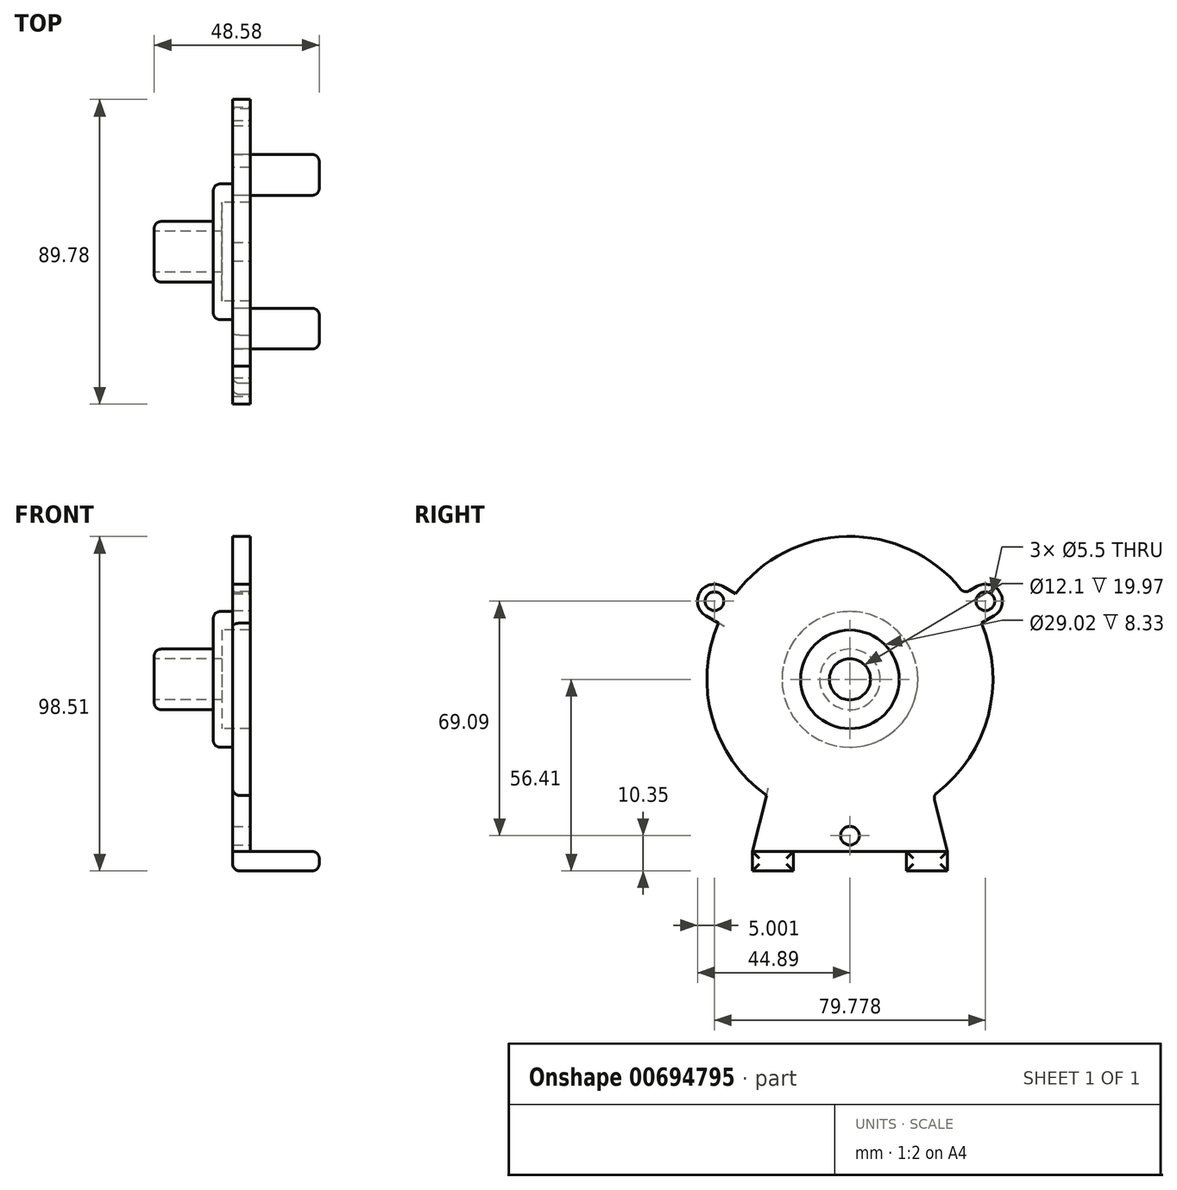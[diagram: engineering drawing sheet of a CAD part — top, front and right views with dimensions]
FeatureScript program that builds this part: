
annotation { "Feature Type Name" : "Feature", "Feature Type Description" : "" }
export const myFeature = defineFeature(function(context is Context, id is Id, definition is map)
    precondition{}
    {
        {
            var Q0;
            Q0=qCreatedBy(makeId("Front.planeOp"),FACE);
            var sketch = newSketch(context, id + "F0", { "sketchPlane" : qUnion([Q0])});
            skLineSegment(sketch, "E0", {"start": v(0, 42.1) * mm, "end": v(-5.2, 42.1) * mm});
            skLineSegment(sketch, "E1", {"start": v(-5.2, 42.1) * mm, "end": v(-5.2, 20) * mm});
            skLineSegment(sketch, "E2", {"start": v(-5.2, 20) * mm, "end": v(-10.9, 20) * mm});
            skLineSegment(sketch, "E3", {"start": v(-10.9, 20) * mm, "end": v(-10.9, 8.92) * mm});
            skLineSegment(sketch, "E4", {"start": v(-10.9, 8.93) * mm, "end": v(-28.3, 8.92) * mm});
            skLineSegment(sketch, "E5", {"start": v(-28.3, 8.92) * mm, "end": v(-28.3, 6.05) * mm});
            skLineSegment(sketch, "E6", {"start": v(-28.3, 6.05) * mm, "end": v(-8.33, 6.05) * mm});
            skLineSegment(sketch, "E7", {"start": v(-8.33, 6.05) * mm, "end": v(-8.33, 14.5) * mm});
            skLineSegment(sketch, "E8", {"start": v(-8.33, 14.5) * mm, "end": v(0, 14.5) * mm});
            skLineSegment(sketch, "E9", {"start": v(0, 14.51) * mm, "end": v(0, 42.1) * mm});
            skLineSegment(sketch, "E10.MirrorCS", {"start": v(-28.3, -8.92) * mm, "end": v(-28.3, -6.05) * mm});
            skLineSegment(sketch, "E11.MirrorCS", {"start": v(0, -14.51) * mm, "end": v(0, -42.1) * mm});
            skLineSegment(sketch, "E12.MirrorCS", {"start": v(-8.33, -14.5) * mm, "end": v(0, -14.5) * mm});
            skLineSegment(sketch, "E13.MirrorCS", {"start": v(-8.33, -6.05) * mm, "end": v(-8.33, -14.5) * mm});
            skLineSegment(sketch, "E14.MirrorCS", {"start": v(-10.9, -20) * mm, "end": v(-10.9, -8.92) * mm});
            skLineSegment(sketch, "E15.MirrorCS", {"start": v(-5.2, -20) * mm, "end": v(-10.9, -20) * mm});
            skLineSegment(sketch, "E16.MirrorCS", {"start": v(-28.3, -6.05) * mm, "end": v(-8.33, -6.05) * mm});
            skLineSegment(sketch, "E17.MirrorCS", {"start": v(-5.2, -42.1) * mm, "end": v(-5.2, -20) * mm});
            skLineSegment(sketch, "E18.MirrorCS", {"start": v(0, -42.1) * mm, "end": v(-5.2, -42.1) * mm});
            skLineSegment(sketch, "E19.MirrorCS", {"start": v(-10.9, -8.93) * mm, "end": v(-28.3, -8.92) * mm});
            skLineSegment(sketch, "E20", {"start": v(-5.2, -42.1) * mm, "end": v(-5.2, -56.41) * mm});
            skLineSegment(sketch, "E21", {"start": v(20.28, -50.7) * mm, "end": v(0, -50.71) * mm});
            skLineSegment(sketch, "E22", {"start": v(20.28, -50.7) * mm, "end": v(20.28, -56.41) * mm});
            skLineSegment(sketch, "E23", {"start": v(-5.2, -56.41) * mm, "end": v(20.28, -56.41) * mm});
            skLineSegment(sketch, "E24", {"start": v(0, -50.71) * mm, "end": v(0, -42.1) * mm});
            skLineSegment(sketch, "E25", {"start": v(-50.44, 0) * mm, "end": v(37.55, 0) * mm});
            skLineSegment(sketch, "E26", {"start": v(-5.2, -20) * mm, "end": v(-5.2, -14.5) * mm});
            skSolve(sketch);
        }
        {
            var Q0;
            Q0=makeQuery(id+"F0.imprint","IMPRINT",FACE,{"disambiguationData":[TD([[makeQuery(id+"F0.imprint","IMPRINT",EDGE,{"derivedFrom":sQuery(id+"F0.wireOp",EDGE,"E0")}),1.0]])]});
            var Q1;
            Q1=sQuery(id+"F0.wireOp",EDGE,"E25");
            revolve(context, id + "F1", {"entities" : qUnion([Q0]), "axis" : qUnion([Q1]), "revolveType" : RevolveType.FULL});
        }
        {
            var Q0;
            Q0=qCreatedBy(makeId("Right.planeOp"),FACE);
            var sketch = newSketch(context, id + "F2", { "sketchPlane" : qUnion([Q0])});
            skArc(sketch, "E27", {"start": v(-33.7, 25.23) * mm, "mid": v(-36.46, 21.05) * mm, "end": v(-38.7, 16.57) * mm});
            skArc(sketch, "E28", {"start": v(-37.39, 27.36) * mm, "mid": v(-44.22, 25.53) * mm, "end": v(-42.39, 18.7) * mm});
            skLineSegment(sketch, "E29", {"start": v(-37.39, 27.36) * mm, "end": v(-33.7, 25.23) * mm});
            skLineSegment(sketch, "E30", {"start": v(-42.39, 18.7) * mm, "end": v(-38.7, 16.57) * mm});
            skLineSegment(sketch, "E31", {"start": v(-39.89, 23.03) * mm, "end": v(0, 0) * mm, "construction": true});
            skCircle(sketch, "E32", {"center": v(-39.89, 23.03) * mm, "radius": 2.75 * mm});
            skLineSegment(sketch, "E33.MirrorCS", {"start": v(42.39, 18.7) * mm, "end": v(38.7, 16.57) * mm});
            skArc(sketch, "E34.MirrorCS", {"start": v(33.7, 25.23) * mm, "mid": v(36.46, 21.05) * mm, "end": v(38.7, 16.57) * mm});
            skArc(sketch, "E35.MirrorCS", {"start": v(37.39, 27.36) * mm, "mid": v(44.22, 25.53) * mm, "end": v(42.39, 18.7) * mm});
            skLineSegment(sketch, "E36.MirrorCS", {"start": v(37.39, 27.36) * mm, "end": v(33.7, 25.23) * mm});
            skCircle(sketch, "E37.MirrorC", {"center": v(39.89, 23.03) * mm, "radius": 2.75 * mm});
            skLineSegment(sketch, "E38.MirrorCS", {"start": v(39.89, 23.03) * mm, "end": v(0, 0) * mm, "construction": true});
            skCircle(sketch, "E39", {"center": v(0, -46.06) * mm, "radius": 2.75 * mm});
            skCircle(sketch, "E40", {"center": v(0, 0) * mm, "radius": 46.06 * mm, "construction": true});
            skLineSegment(sketch, "E41", {"start": v(-24.57, -34.19) * mm, "end": v(-28.65, -50.71) * mm});
            skLineSegment(sketch, "E42", {"start": v(-28.65, -50.71) * mm, "end": v(-28.65, -56.41) * mm});
            skLineSegment(sketch, "E43", {"start": v(-28.65, -56.41) * mm, "end": v(-16.65, -56.41) * mm});
            skLineSegment(sketch, "E44", {"start": v(-28.65, -50.71) * mm, "end": v(28.65, -50.71) * mm});
            skLineSegment(sketch, "E45.MirrorCS", {"start": v(24.57, -34.19) * mm, "end": v(28.65, -50.71) * mm});
            skLineSegment(sketch, "E46.MirrorCS", {"start": v(28.65, -50.71) * mm, "end": v(28.65, -56.41) * mm});
            skArc(sketch, "E47", {"start": v(-24.57, -34.19) * mm, "mid": v(0, -42.1) * mm, "end": v(24.57, -34.19) * mm});
            skLineSegment(sketch, "E48", {"start": v(-16.65, -50.71) * mm, "end": v(-16.65, -56.41) * mm});
            skLineSegment(sketch, "E49.MirrorCS", {"start": v(16.65, -50.71) * mm, "end": v(16.65, -56.41) * mm});
            skLineSegment(sketch, "E50.trimOffspring", {"start": v(16.65, -56.41) * mm, "end": v(28.65, -56.41) * mm});
            skSolve(sketch);
        }
        {
            var Q0;
            Q0=makeQuery(id+"F2.imprint","IMPRINT",FACE,{"disambiguationData":[TD([[makeQuery(id+"F2.imprint","IMPRINT",EDGE,{"derivedFrom":sQuery(id+"F2.wireOp",EDGE,"E27")}),-1.0]])]});
            var Q1;
            Q1=makeQuery(id+"F1.opRevolve","SWEPT_FACE",FACE,{"disambiguationData":[OSD([sQuery(id+"F0.wireOp",EDGE,"E1")])]});
            extrude(context, id + "F3", {"entities" : qUnion([Q0]), "operationType" : NewBodyOperationType.ADD, "endBound" : BoundingType.UP_TO_SURFACE, "oppositeDirection" : true, "endBoundEntityFace" : qUnion([Q1]), "depth" : 25 * mm});
        }
        {
            var Q0;
            Q0=makeQuery(id+"F2.imprint","IMPRINT",FACE,{"disambiguationData":[TD([[makeQuery(id+"F2.imprint","IMPRINT",EDGE,{"derivedFrom":sQuery(id+"F2.wireOp",EDGE,"E33.MirrorCS")}),-1.0]])]});
            var Q1;
            Q1=makeQuery(id+"F3.boolean.opBoolean","MERGE",FACE,{"derivedFrom":[makeQuery(id+"F1.opRevolve","SWEPT_FACE",FACE,{"disambiguationData":[OSD([sQuery(id+"F0.wireOp",EDGE,"E1")])]}),makeQuery(id+"F3.opExtrude","CAP_FACE",FACE,{"disambiguationData":[OSD([sQuery(id+"F2.wireOp",EDGE,"E27"),sQuery(id+"F2.wireOp",EDGE,"E28"),sQuery(id+"F2.wireOp",EDGE,"E29"),sQuery(id+"F2.wireOp",EDGE,"E30"),sQuery(id+"F2.wireOp",EDGE,"E32")])],"isStart":false})]});
            extrude(context, id + "F4", {"entities" : qUnion([Q0]), "operationType" : NewBodyOperationType.ADD, "endBound" : BoundingType.UP_TO_SURFACE, "oppositeDirection" : true, "endBoundEntityFace" : qUnion([Q1]), "depth" : 25 * mm});
        }
        {
            var Q0;
            Q0=makeQuery(id+"F2.imprint","IMPRINT",FACE,{"disambiguationData":[TD([[makeQuery(id+"F2.imprint","IMPRINT",EDGE,{"derivedFrom":sQuery(id+"F2.wireOp",EDGE,"E39")}),-1.0]])]});
            var Q1;
            Q1=makeQuery(id+"F4.boolean.opBoolean","MERGE",FACE,{"derivedFrom":[makeQuery(id+"F3.boolean.opBoolean","MERGE",FACE,{"derivedFrom":[makeQuery(id+"F1.opRevolve","SWEPT_FACE",FACE,{"disambiguationData":[OSD([sQuery(id+"F0.wireOp",EDGE,"E1")])]}),makeQuery(id+"F3.opExtrude","CAP_FACE",FACE,{"disambiguationData":[OSD([sQuery(id+"F2.wireOp",EDGE,"E27"),sQuery(id+"F2.wireOp",EDGE,"E28"),sQuery(id+"F2.wireOp",EDGE,"E29"),sQuery(id+"F2.wireOp",EDGE,"E30"),sQuery(id+"F2.wireOp",EDGE,"E32")])],"isStart":false})]}),makeQuery(id+"F4.opExtrude","CAP_FACE",FACE,{"disambiguationData":[OSD([sQuery(id+"F2.wireOp",EDGE,"E33.MirrorCS"),sQuery(id+"F2.wireOp",EDGE,"E34.MirrorCS"),sQuery(id+"F2.wireOp",EDGE,"E35.MirrorCS"),sQuery(id+"F2.wireOp",EDGE,"E36.MirrorCS"),sQuery(id+"F2.wireOp",EDGE,"E37.MirrorC")])],"isStart":false})]});
            extrude(context, id + "F5", {"entities" : qUnion([Q0]), "operationType" : NewBodyOperationType.ADD, "endBound" : BoundingType.UP_TO_SURFACE, "oppositeDirection" : true, "endBoundEntityFace" : qUnion([Q1]), "depth" : 25 * mm});
        }
        {
            var Q0;
            Q0=makeQuery(id+"F2.imprint","IMPRINT",FACE,{"disambiguationData":[TD([[makeQuery(id+"F2.imprint","IMPRINT",EDGE,{"derivedFrom":sQuery(id+"F2.wireOp",EDGE,"E42")}),1.0]])]});
            var Q1;
            {var subQ0=sQuery(id+"F2.wireOp",EDGE,"E46.MirrorCS");Q1=makeQuery(id+"F2.imprint","IMPRINT",FACE,{"disambiguationData":[TD([[makeQuery(id+"F2.imprint","IMPRINT",EDGE,{"derivedFrom":subQ0}),-1.0]])]});}
            var Q2;
            Q2=sQuery(id+"F0.wireOp",VERTEX,"E22.start");
            var Q3;
            Q3=sQuery(id+"F0.wireOp",VERTEX,"E20.end");
            extrude(context, id + "F6", {"entities" : qUnion([Q0, Q1]), "operationType" : NewBodyOperationType.ADD, "endBound" : BoundingType.UP_TO_VERTEX, "endBoundEntityVertex" : qUnion([Q2]), "depth" : 25 * mm, "hasSecondDirection" : true, "secondDirectionBound" : SecondDirectionBoundingType.UP_TO_VERTEX, "secondDirectionOppositeDirection" : true, "secondDirectionBoundEntityVertex" : qUnion([Q3]), "secondDirectionDepth" : 25 * mm});
        }
        {
            var Q0;
            Q0=makeQuery(id+"F1.opRevolve","SWEPT_EDGE",EDGE,{"disambiguationData":[OSD([sQuery(id+"F0.wireOp",EDGE,"E2"),sQuery(id+"F0.wireOp",EDGE,"E3")])]});
            var Q1;
            Q1=makeQuery(id+"F1.opRevolve","SWEPT_EDGE",EDGE,{"disambiguationData":[OSD([sQuery(id+"F0.wireOp",EDGE,"E4"),sQuery(id+"F0.wireOp",EDGE,"E5")])]});
            var Q2;
            Q2=makeQuery(id+"F3.opExtrude","SWEPT_EDGE",EDGE,{"disambiguationData":[OSD([sQuery(id+"F2.wireOp",EDGE,"E27"),sQuery(id+"F2.wireOp",EDGE,"E29")])]});
            var Q3;
            Q3=makeQuery(id+"F3.opExtrude","SWEPT_EDGE",EDGE,{"disambiguationData":[OSD([sQuery(id+"F2.wireOp",EDGE,"E27"),sQuery(id+"F2.wireOp",EDGE,"E30")])]});
            var Q4;
            Q4=makeQuery(id+"F4.opExtrude","SWEPT_EDGE",EDGE,{"disambiguationData":[OSD([sQuery(id+"F2.wireOp",EDGE,"E34.MirrorCS"),sQuery(id+"F2.wireOp",EDGE,"E36.MirrorCS")])]});
            var Q5;
            Q5=makeQuery(id+"F4.opExtrude","SWEPT_EDGE",EDGE,{"disambiguationData":[OSD([sQuery(id+"F2.wireOp",EDGE,"E33.MirrorCS"),sQuery(id+"F2.wireOp",EDGE,"E34.MirrorCS")])]});
            var Q6;
            Q6=makeQuery(id+"F5.opExtrude","SWEPT_EDGE",EDGE,{"disambiguationData":[OSD([sQuery(id+"F2.wireOp",EDGE,"E45.MirrorCS"),sQuery(id+"F2.wireOp",EDGE,"E47")])]});
            var Q7;
            Q7=makeQuery(id+"F5.opExtrude","SWEPT_EDGE",EDGE,{"disambiguationData":[OSD([sQuery(id+"F2.wireOp",EDGE,"E41"),sQuery(id+"F2.wireOp",EDGE,"E47")])]});
            var Q8;
            {var subQ0=sQuery(id+"F2.wireOp",EDGE,"E30");var subQ1=makeQuery(id+"F3.opExtrude","SWEPT_FACE",FACE,{"disambiguationData":[OSD([subQ0])]});var subQ2=sQuery(id+"F0.wireOp",EDGE,"E1");var subQ5=sQuery(id+"F0.wireOp",EDGE,"E0");Q8=makeQuery(id+"F5.boolean.opBoolean","SPLIT",EDGE,{"disambiguationData":[TD([subQ1])],"derivedFrom":makeQuery(id+"F4.boolean.opBoolean","SPLIT",EDGE,{"disambiguationData":[TD([subQ1])],"derivedFrom":makeQuery(id+"F1.opRevolve","SWEPT_EDGE",EDGE,{"disambiguationData":[OSD([subQ5,subQ2])]})})});}
            var Q9;
            Q9=makeQuery(id+"F6.opExtrude","CAP_EDGE",EDGE,{"disambiguationData":[OSD([sQuery(id+"F2.wireOp",EDGE,"E42")])],"isStart":false});
            var Q10;
            Q10=makeQuery(id+"F6.opExtrude","CAP_EDGE",EDGE,{"disambiguationData":[OSD([sQuery(id+"F2.wireOp",EDGE,"E48")])],"isStart":false});
            var Q11;
            Q11=makeQuery(id+"F6.opExtrude","CAP_EDGE",EDGE,{"disambiguationData":[OSD([sQuery(id+"F2.wireOp",EDGE,"E49.MirrorCS")])],"isStart":false});
            var Q12;
            Q12=makeQuery(id+"F6.opExtrude","CAP_EDGE",EDGE,{"disambiguationData":[OSD([sQuery(id+"F2.wireOp",EDGE,"E46.MirrorCS")])],"isStart":false});
            var Q13;
            {var subQ0=sQuery(id+"F2.wireOp",EDGE,"E44");var subQ1=sQuery(id+"F2.wireOp",EDGE,"E42");Q13=makeQuery(id+"F6.boolean.opBoolean","SPLIT",EDGE,{"derivedFrom":makeQuery(id+"F6.opExtrude","TWEAK_EDGE",EDGE,{"derivedFrom":[makeQuery(id+"F2.imprint","IMPRINT",EDGE,{"derivedFrom":subQ1}),makeQuery(id+"F2.imprint","IMPRINT",EDGE,{"disambiguationData":[TD([[makeQuery(id+"F2.imprint","INTERSECT",VERTEX,{"derivedFrom":[subQ0,sQuery(id+"F2.wireOp",EDGE,"E48")]}),1.0]])],"derivedFrom":subQ0})]})});}
            var Q14;
            {var subQ0=sQuery(id+"F2.wireOp",EDGE,"E44");Q14=makeQuery(id+"F6.opExtrude","CAP_EDGE",EDGE,{"disambiguationData":[OSD([subQ0]),TDD([makeQuery(id+"F2.imprint","IMPRINT",EDGE,{"disambiguationData":[TD([[makeQuery(id+"F2.imprint","INTERSECT",VERTEX,{"derivedFrom":[subQ0,sQuery(id+"F2.wireOp",EDGE,"E48")]}),1.0]])],"derivedFrom":subQ0})])],"isStart":false});}
            var Q15;
            {var subQ0=sQuery(id+"F2.wireOp",EDGE,"E44");var subQ1=sQuery(id+"F2.wireOp",EDGE,"E48");var subQ2=makeQuery(id+"F2.imprint","IMPRINT",EDGE,{"disambiguationData":[TD([[makeQuery(id+"F2.imprint","INTERSECT",VERTEX,{"derivedFrom":[subQ0,subQ1]}),1.0]])],"derivedFrom":subQ0});Q15=makeQuery(id+"F6.boolean.opBoolean","SPLIT",EDGE,{"disambiguationData":[topologyDisambiguationEdgeConnected([makeQuery(id+"F6.opExtrude","SWEPT_FACE",FACE,{"disambiguationData":[OSD([subQ0]),TDD([subQ2])]})])],"derivedFrom":makeQuery(id+"F6.opExtrude","TWEAK_EDGE",EDGE,{"derivedFrom":[subQ2,makeQuery(id+"F2.imprint","IMPRINT",EDGE,{"derivedFrom":subQ1})]})});}
            var Q16;
            {var subQ0=sQuery(id+"F2.wireOp",EDGE,"E44");var subQ1=sQuery(id+"F2.wireOp",EDGE,"E49.MirrorCS");var subQ2=makeQuery(id+"F2.imprint","IMPRINT",EDGE,{"disambiguationData":[TD([[makeQuery(id+"F2.imprint","INTERSECT",VERTEX,{"derivedFrom":[subQ0,subQ1]}),-1.0]])],"derivedFrom":subQ0});Q16=makeQuery(id+"F6.boolean.opBoolean","SPLIT",EDGE,{"disambiguationData":[topologyDisambiguationEdgeConnected([makeQuery(id+"F6.opExtrude","SWEPT_FACE",FACE,{"disambiguationData":[OSD([subQ0]),TDD([subQ2])]})])],"derivedFrom":makeQuery(id+"F6.opExtrude","TWEAK_EDGE",EDGE,{"derivedFrom":[subQ2,makeQuery(id+"F2.imprint","IMPRINT",EDGE,{"derivedFrom":subQ1})]})});}
            var Q17;
            {var subQ0=sQuery(id+"F2.wireOp",EDGE,"E44");Q17=makeQuery(id+"F6.opExtrude","CAP_EDGE",EDGE,{"disambiguationData":[OSD([subQ0]),TDD([makeQuery(id+"F2.imprint","IMPRINT",EDGE,{"disambiguationData":[TD([[makeQuery(id+"F2.imprint","INTERSECT",VERTEX,{"derivedFrom":[subQ0,sQuery(id+"F2.wireOp",EDGE,"E49.MirrorCS")]}),-1.0]])],"derivedFrom":subQ0})])],"isStart":false});}
            var Q18;
            {var subQ0=sQuery(id+"F2.wireOp",EDGE,"E46.MirrorCS");var subQ1=sQuery(id+"F2.wireOp",EDGE,"E44");Q18=makeQuery(id+"F6.boolean.opBoolean","SPLIT",EDGE,{"derivedFrom":makeQuery(id+"F6.opExtrude","TWEAK_EDGE",EDGE,{"derivedFrom":[makeQuery(id+"F2.imprint","IMPRINT",EDGE,{"disambiguationData":[TD([[makeQuery(id+"F2.imprint","INTERSECT",VERTEX,{"derivedFrom":[subQ1,sQuery(id+"F2.wireOp",EDGE,"E49.MirrorCS")]}),-1.0]])],"derivedFrom":subQ1}),makeQuery(id+"F2.imprint","IMPRINT",EDGE,{"derivedFrom":subQ0})]})});}
            var Q19;
            Q19=makeQuery(id+"F6.opExtrude","TWEAK_EDGE",EDGE,{"derivedFrom":[makeQuery(id+"F2.imprint","IMPRINT",EDGE,{"derivedFrom":sQuery(id+"F2.wireOp",EDGE,"E42")}),makeQuery(id+"F2.imprint","IMPRINT",EDGE,{"derivedFrom":sQuery(id+"F2.wireOp",EDGE,"E43")})]});
            var Q20;
            Q20=makeQuery(id+"F6.opExtrude","TWEAK_EDGE",EDGE,{"derivedFrom":[makeQuery(id+"F2.imprint","IMPRINT",EDGE,{"derivedFrom":sQuery(id+"F2.wireOp",EDGE,"E46.MirrorCS")}),makeQuery(id+"F2.imprint","IMPRINT",EDGE,{"derivedFrom":sQuery(id+"F2.wireOp",EDGE,"E50.trimOffspring")})]});
            var Q21;
            Q21=makeQuery(id+"F6.opExtrude","CAP_EDGE",EDGE,{"disambiguationData":[OSD([sQuery(id+"F2.wireOp",EDGE,"E50.trimOffspring")])],"isStart":false});
            var Q22;
            Q22=makeQuery(id+"F6.opExtrude","TWEAK_EDGE",EDGE,{"derivedFrom":[makeQuery(id+"F2.imprint","IMPRINT",EDGE,{"derivedFrom":sQuery(id+"F2.wireOp",EDGE,"E49.MirrorCS")}),makeQuery(id+"F2.imprint","IMPRINT",EDGE,{"derivedFrom":sQuery(id+"F2.wireOp",EDGE,"E50.trimOffspring")})]});
            var Q23;
            Q23=makeQuery(id+"F6.opExtrude","CAP_EDGE",EDGE,{"disambiguationData":[OSD([sQuery(id+"F2.wireOp",EDGE,"E43")])],"isStart":false});
            var Q24;
            Q24=makeQuery(id+"F6.opExtrude","TWEAK_EDGE",EDGE,{"derivedFrom":[makeQuery(id+"F2.imprint","IMPRINT",EDGE,{"derivedFrom":sQuery(id+"F2.wireOp",EDGE,"E43")}),makeQuery(id+"F2.imprint","IMPRINT",EDGE,{"derivedFrom":sQuery(id+"F2.wireOp",EDGE,"E48")})]});
            var Q25;
            Q25=makeQuery(id+"F6.opExtrude","CAP_EDGE",EDGE,{"disambiguationData":[OSD([sQuery(id+"F2.wireOp",EDGE,"E43")])],"isStart":true});
            var Q26;
            Q26=makeQuery(id+"F6.opExtrude","CAP_EDGE",EDGE,{"disambiguationData":[OSD([sQuery(id+"F2.wireOp",EDGE,"E50.trimOffspring")])],"isStart":true});
            fillet(context, id + "F7", {"entities" : qUnion([Q0, Q1, Q2, Q3, Q4, Q5, Q6, Q7, Q8, Q9, Q10, Q11, Q12, Q13, Q14, Q15, Q16, Q17, Q18, Q19, Q20, Q21, Q22, Q23, Q24, Q25, Q26]), "radius" : 2 * mm, "tangentPropagation" : true, "allowEdgeOverflow" : false});
        }
    });
